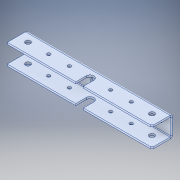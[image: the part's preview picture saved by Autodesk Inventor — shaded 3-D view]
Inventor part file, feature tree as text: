
AUTODESK INVENTOR PART (.ipt)
format: ipt  version: 2017 (Build 210142000, 142)  size: 301,056 bytes
history: native  units: in
note: dims shown in document units (in); Inventor stores cm internally (conversion verified against a paired STEP export)
features: sketch x5, hole x4, split x1, extrude x1, other x1
ambient origin geometry x8: Origin, YZ Plane, XZ Plane, XY Plane, X Axis, Y Axis, Z Axis, Center Point
bodies: Solid1 (feature_tree)
feature tree (12):
  split  "Split1"
  hole  "Hole1"  [1 undecoded]
  sketch  "Sketch3"  dims[d19=1.0in d20=0.0in]
  extrude  "Extrusion2"  Depth=0.375in
  hole  "Hole3"  [1 undecoded]
  hole  "Hole4"  [1 undecoded]
  hole  "Hole5"  [1 undecoded]
  sketch  "Sketch1"  dims[d0=0.25in d1=0.25in]
  sketch  "Sketch2"  dims[d2=0.25in d3=0.75in d4=0.375in d5=0.25in d6=0.5635in d7=1.0in d8=0.8108in d9=0.375in]
  sketch  "Sketch4"  dims[d21=0.375in d22=0.75in d23=0.375in d24=0.25in d25=0.5635in d26=1.0in d27=0.8108in d28=0.75in]
  sketch  "Sketch5"  dims[d29=0.75in d30=0.75in d31=0.375in d32=0.25in d33=0.5635in d34=1.0in d35=0.8108in d36=0.25in d37=0.25in d38=0.25in d39=0.75in d40=0.375in d41=0.25in d42=0.5635in d43=1.0in d44=0.8108in]
  other  "Break-Corner1"
note: 4 required parameter values undecoded (feature->parameter linkage not recoverable at this tier; creation-order binding heuristic only, values carry confidence <= 0.55)
